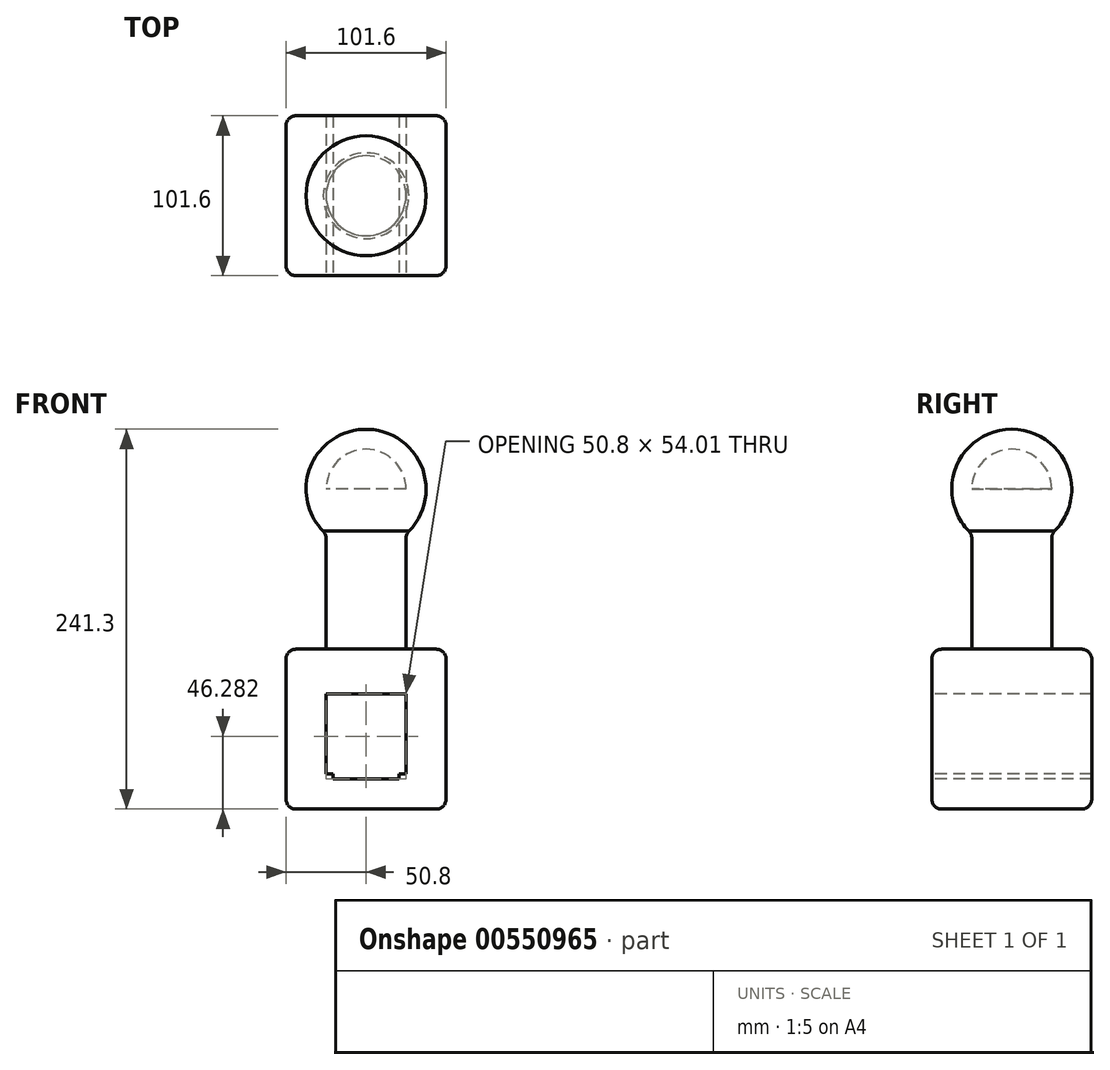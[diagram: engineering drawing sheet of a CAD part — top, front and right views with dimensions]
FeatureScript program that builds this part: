
annotation { "Feature Type Name" : "Feature", "Feature Type Description" : "" }
export const myFeature = defineFeature(function(context is Context, id is Id, definition is map)
    precondition{}
    {
        {
            var Q0;
            Q0=qCreatedBy(makeId("Top.planeOp"),FACE);
            var sketch = newSketch(context, id + "F0", { "sketchPlane" : qUnion([Q0])});
            skLineSegment(sketch, "E0.bottom", {"start": v(50.8, -50.8) * mm, "end": v(-50.8, -50.8) * mm});
            skLineSegment(sketch, "E0.top", {"start": v(50.8, 50.8) * mm, "end": v(-50.8, 50.8) * mm});
            skLineSegment(sketch, "E0.left", {"start": v(50.8, -50.8) * mm, "end": v(50.8, 50.8) * mm});
            skLineSegment(sketch, "E0.right", {"start": v(-50.8, -50.8) * mm, "end": v(-50.8, 50.8) * mm});
            skPoint(sketch, "E0.middle", {"position": v(0, 0) * mm});
            skSolve(sketch);
        }
        {
            var Q0;
            Q0 = qSketchRegion(id + "F0", true);
            extrude(context, id + "F1", {"entities" : qUnion([Q0]), "depth" : 101.6 * mm, "offsetDistance" : 25.4 * mm});
        }
        {
            var Q0;
            Q0=makeQuery(id+"F1.opExtrude","CAP_FACE",FACE,{"disambiguationData":[OSD([sQuery(id+"F0.wireOp",EDGE,"E0.bottom"),sQuery(id+"F0.wireOp",EDGE,"E0.top"),sQuery(id+"F0.wireOp",EDGE,"E0.left"),sQuery(id+"F0.wireOp",EDGE,"E0.right")])],"isStart":false});
            var sketch = newSketch(context, id + "F2", { "sketchPlane" : qUnion([Q0])});
            skCircle(sketch, "E1", {"center": v(0, 0) * mm, "radius": 25.4 * mm});
            skSolve(sketch);
        }
        {
            var Q0;
            Q0 = qSketchRegion(id + "F2", true);
            extrude(context, id + "F3", {"entities" : qUnion([Q0]), "operationType" : NewBodyOperationType.ADD, "flatOperationType" : FlatOperationType.REMOVE, "depth" : 101.6 * mm, "offsetDistance" : 25.4 * mm, "domain" : OperationDomain.MODEL});
        }
        {
            var Q0;
            Q0=makeQuery(id+"F3.opExtrude","CAP_FACE",FACE,{"disambiguationData":[OSD([sQuery(id+"F2.wireOp",EDGE,"E1")])],"isStart":false});
            var sketch = newSketch(context, id + "F4", { "sketchPlane" : qUnion([Q0])});
            skArc(sketch, "E2", {"start": v(0, -38.1) * mm, "mid": v(38.1, 0) * mm, "end": v(0, 38.1) * mm});
            skLineSegment(sketch, "E3", {"start": v(0, 0) * mm, "end": v(0, -38.1) * mm});
            skLineSegment(sketch, "E4", {"start": v(0, -38.1) * mm, "end": v(0, 38.1) * mm});
            skSolve(sketch);
        }
        {
            var Q0;
            {var subQ0=sQuery(id+"F4.wireOp",EDGE,"E2");Q0=makeQuery(id+"F4.imprint","IMPRINT",FACE,{"disambiguationData":[TD([[makeQuery(id+"F4.imprint","IMPRINT",EDGE,{"derivedFrom":subQ0}),1.0]])]});}
            var Q1;
            {var subQ0=sQuery(id+"F4.wireOp",EDGE,"E4");var subQ1=makeQuery(id+"F4.imprint","IMPRINT",VERTEX,{"derivedFrom":subQ0});Q1=makeQuery(id+"F4.imprint","IMPRINT",FACE,{"disambiguationData":[TD([[makeQuery(id+"F4.imprint","IMPRINT",EDGE,{"disambiguationData":[TD([[subQ1,1.0]])],"derivedFrom":subQ0}),-1.0]])]});}
            var Q2;
            Q2=sQuery(id+"F4.wireOp",EDGE,"E4");
            revolve(context, id + "F5", {"operationType" : NewBodyOperationType.ADD, "entities" : qUnion([Q0, Q1]), "axis" : qUnion([Q2]), "revolveType" : RevolveType.FULL});
        }
        {
            var Q0;
            Q0=makeQuery(id+"F1.opExtrude","SWEPT_FACE",FACE,{"disambiguationData":[OSD([sQuery(id+"F0.wireOp",EDGE,"E0.bottom")])]});
            var sketch = newSketch(context, id + "F6", { "sketchPlane" : qUnion([Q0])});
            skLineSegment(sketch, "E5.bottom", {"start": v(21.06, 19.28) * mm, "end": v(-21.06, 19.28) * mm});
            skLineSegment(sketch, "E5.top", {"start": v(21.06, 71.47) * mm, "end": v(-21.06, 71.47) * mm});
            skLineSegment(sketch, "E5.left", {"start": v(21.06, 19.28) * mm, "end": v(21.06, 71.47) * mm});
            skLineSegment(sketch, "E5.right", {"start": v(-21.06, 19.28) * mm, "end": v(-21.06, 71.47) * mm});
            skPoint(sketch, "E5.middle", {"position": v(0, 45.38) * mm});
            skSolve(sketch);
        }
        {
            var Q0;
            Q0=makeQuery(id+"F6.imprint","IMPRINT",FACE,{"disambiguationData":[TD([[makeQuery(id+"F6.imprint","IMPRINT",EDGE,{"derivedFrom":sQuery(id+"F6.wireOp",EDGE,"E5.bottom")}),-1.0]])]});
            var sketch = newSketch(context, id + "F7", { "sketchPlane" : qUnion([Q0])});
            skLineSegment(sketch, "E6.bottom", {"start": v(-25.4, 73.29) * mm, "end": v(25.4, 73.29) * mm});
            skLineSegment(sketch, "E6.top", {"start": v(-25.4, 22.49) * mm, "end": v(25.4, 22.49) * mm});
            skLineSegment(sketch, "E6.left", {"start": v(-25.4, 73.29) * mm, "end": v(-25.4, 22.49) * mm});
            skLineSegment(sketch, "E6.right", {"start": v(25.4, 73.29) * mm, "end": v(25.4, 22.49) * mm});
            skPoint(sketch, "E6.middle", {"position": v(0, 47.89) * mm});
            skSolve(sketch);
        }
        {
            var Q0;
            Q0=makeQuery(id+"F6.imprint","IMPRINT",FACE,{"disambiguationData":[TD([[makeQuery(id+"F6.imprint","IMPRINT",EDGE,{"derivedFrom":sQuery(id+"F6.wireOp",EDGE,"E5.bottom")}),-1.0]])]});
            extrude(context, id + "F8", {"entities" : qUnion([Q0]), "operationType" : NewBodyOperationType.REMOVE, "oppositeDirection" : true, "depth" : 101.6 * mm, "offsetDistance" : 25.4 * mm});
        }
        {
            var Q0;
            Q0=makeQuery(id+"F1.opExtrude","CAP_EDGE",EDGE,{"disambiguationData":[OSD([sQuery(id+"F0.wireOp",EDGE,"E0.left")])],"isStart":false});
            var Q1;
            Q1=makeQuery(id+"F1.opExtrude","SWEPT_EDGE",EDGE,{"disambiguationData":[OSD([sQuery(id+"F0.wireOp",EDGE,"E0.bottom"),sQuery(id+"F0.wireOp",EDGE,"E0.left")])]});
            var Q2;
            Q2=makeQuery(id+"F1.opExtrude","SWEPT_EDGE",EDGE,{"disambiguationData":[OSD([sQuery(id+"F0.wireOp",EDGE,"E0.top"),sQuery(id+"F0.wireOp",EDGE,"E0.left")])]});
            var Q3;
            Q3=makeQuery(id+"F1.opExtrude","CAP_EDGE",EDGE,{"disambiguationData":[OSD([sQuery(id+"F0.wireOp",EDGE,"E0.left")])],"isStart":true});
            var Q4;
            Q4=makeQuery(id+"F1.opExtrude","CAP_EDGE",EDGE,{"disambiguationData":[OSD([sQuery(id+"F0.wireOp",EDGE,"E0.right")])],"isStart":false});
            var Q5;
            Q5=makeQuery(id+"F1.opExtrude","CAP_EDGE",EDGE,{"disambiguationData":[OSD([sQuery(id+"F0.wireOp",EDGE,"E0.bottom")])],"isStart":false});
            var Q6;
            Q6=makeQuery(id+"F1.opExtrude","SWEPT_EDGE",EDGE,{"disambiguationData":[OSD([sQuery(id+"F0.wireOp",EDGE,"E0.bottom"),sQuery(id+"F0.wireOp",EDGE,"E0.right")])]});
            var Q7;
            Q7=makeQuery(id+"F1.opExtrude","CAP_EDGE",EDGE,{"disambiguationData":[OSD([sQuery(id+"F0.wireOp",EDGE,"E0.top")])],"isStart":false});
            var Q8;
            Q8=makeQuery(id+"F1.opExtrude","CAP_EDGE",EDGE,{"disambiguationData":[OSD([sQuery(id+"F0.wireOp",EDGE,"E0.bottom")])],"isStart":true});
            var Q9;
            Q9=makeQuery(id+"F1.opExtrude","CAP_EDGE",EDGE,{"disambiguationData":[OSD([sQuery(id+"F0.wireOp",EDGE,"E0.top")])],"isStart":true});
            var Q10;
            Q10=makeQuery(id+"F1.opExtrude","CAP_EDGE",EDGE,{"disambiguationData":[OSD([sQuery(id+"F0.wireOp",EDGE,"E0.right")])],"isStart":true});
            var Q11;
            Q11=makeQuery(id+"F1.opExtrude","SWEPT_EDGE",EDGE,{"disambiguationData":[OSD([sQuery(id+"F0.wireOp",EDGE,"E0.top"),sQuery(id+"F0.wireOp",EDGE,"E0.right")])]});
            var Q12;
            Q12=makeQuery(id+"F5.boolean.opBoolean","INTERSECT",EDGE,{"derivedFrom":[makeQuery(id+"F3.opExtrude","SWEPT_FACE",FACE,{"disambiguationData":[OSD([sQuery(id+"F2.wireOp",EDGE,"E1")])]}),makeQuery(id+"F5.opRevolve","SWEPT_FACE",FACE,{"disambiguationData":[OSD([sQuery(id+"F4.wireOp",EDGE,"E2")])]})]});
            var Q13;
            Q13=makeQuery(id+"F3.opExtrude","CAP_EDGE",EDGE,{"disambiguationData":[OSD([sQuery(id+"F2.wireOp",EDGE,"E1")])],"isStart":true});
            fillet(context, id + "F9", {"entities" : qUnion([Q0, Q1, Q2, Q3, Q4, Q5, Q6, Q7, Q8, Q9, Q10, Q11, Q12, Q13]), "radius" : 6.35 * mm, "tangentPropagation" : true, "allowEdgeOverflow" : false});
        }
        {
            var Q0;
            Q0=makeQuery(id+"F7.imprint","IMPRINT",FACE,{"disambiguationData":[TD([[makeQuery(id+"F7.imprint","IMPRINT",EDGE,{"derivedFrom":sQuery(id+"F7.wireOp",EDGE,"E6.bottom")}),-1.0]])]});
            extrude(context, id + "F10", {"entities" : qUnion([Q0]), "operationType" : NewBodyOperationType.REMOVE, "oppositeDirection" : true, "depth" : 25.4 * mm, "offsetDistance" : 25.4 * mm});
        }
        {
            var Q0;
            Q0 = qSketchRegion(id + "F7", true);
            extrude(context, id + "F11", {"entities" : qUnion([Q0]), "operationType" : NewBodyOperationType.REMOVE, "oppositeDirection" : true, "depth" : 127 * mm, "offsetDistance" : 25.4 * mm});
        }
    });
